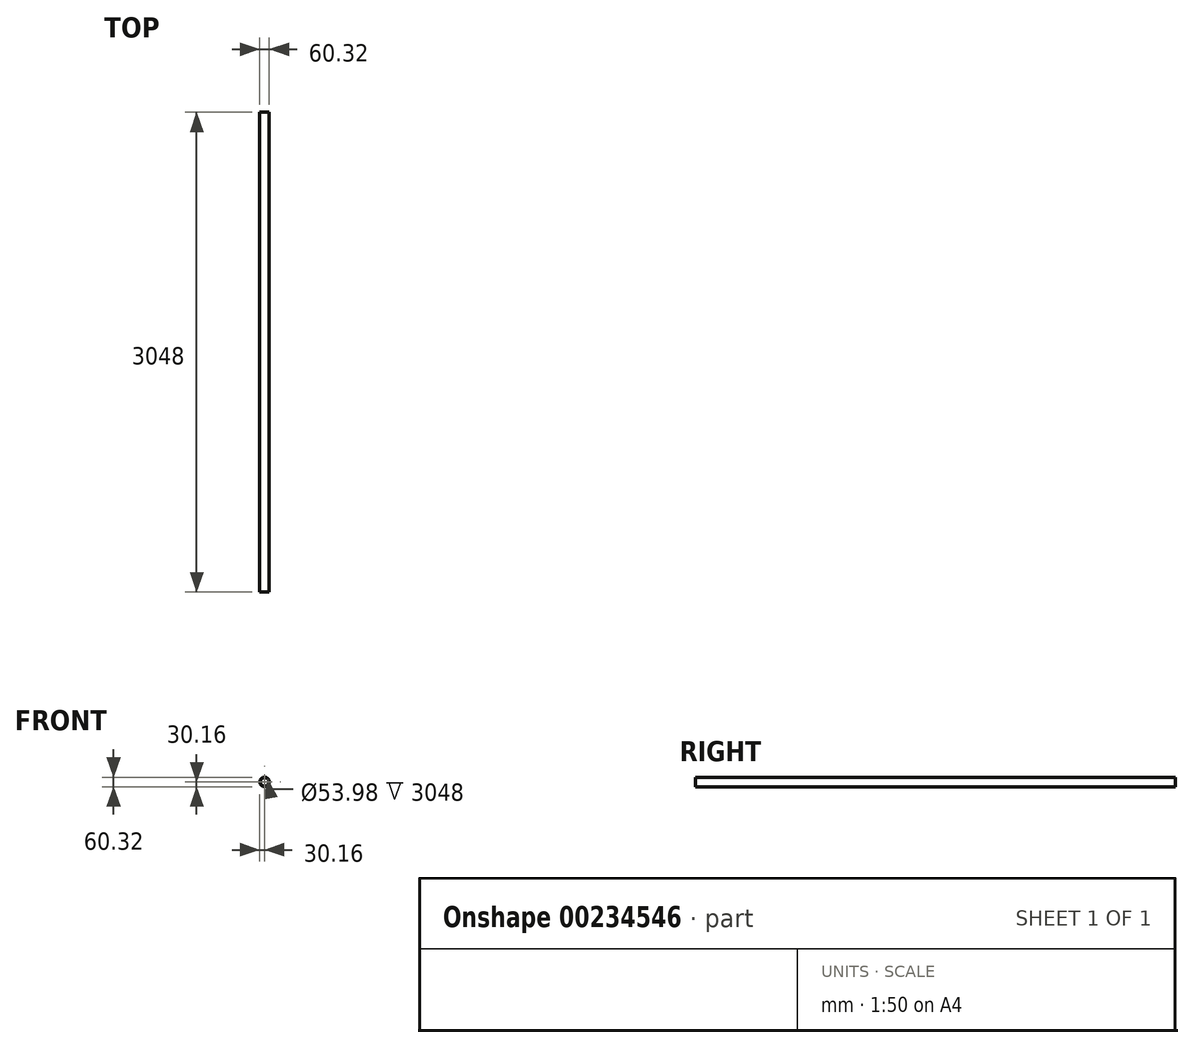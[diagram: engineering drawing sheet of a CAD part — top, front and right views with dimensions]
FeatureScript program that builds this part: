
annotation { "Feature Type Name" : "Feature", "Feature Type Description" : "" }
export const myFeature = defineFeature(function(context is Context, id is Id, definition is map)
    precondition{}
    {
        {
            var Q0;
            Q0=qCreatedBy(makeId("Top.planeOp"),FACE);
            var sketch = newSketch(context, id + "F0", { "sketchPlane" : qUnion([Q0])});
            skLineSegment(sketch, "E0", {"start": v(0, 0) * mm, "end": v(0, 3048) * mm});
            skSolve(sketch);
        }
        {
            var Q0;
            Q0=qCreatedBy(makeId("Front.planeOp"),FACE);
            var sketch = newSketch(context, id + "F1", { "sketchPlane" : qUnion([Q0])});
            skCircle(sketch, "E1", {"center": v(0, 0) * mm, "radius": 30.16 * mm});
            skCircle(sketch, "E2", {"center": v(0, 0) * mm, "radius": 26.99 * mm});
            skSolve(sketch);
        }
        {
            var Q0;
            Q0 = qSketchRegion(id + "F1", true);
            var Q1;
            Q1 = qConstructionFilter(qBodyType(qCreatedBy(id + "F0" ,EDGE), BodyType.WIRE), ConstructionObject.NO);
            sweep(context, id + "F2", {"profiles" : qUnion([Q0]), "path" : qUnion([Q1])});
        }
    });
